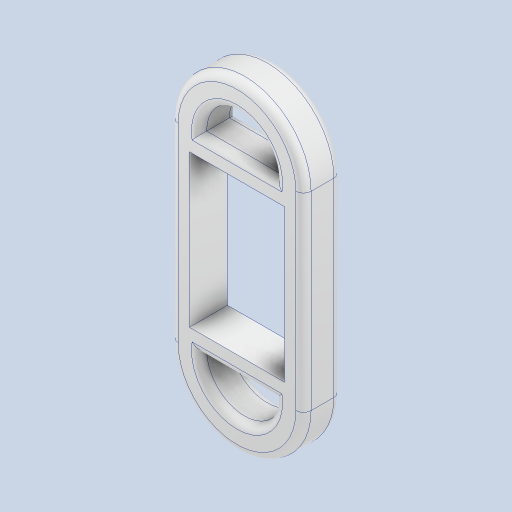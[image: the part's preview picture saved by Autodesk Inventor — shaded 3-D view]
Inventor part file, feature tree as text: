
AUTODESK INVENTOR PART (.ipt)
format: ipt  version: 2024 (Build 280153000, 153)  size: 239,104 bytes
history: native  units: mm
features: other x1, extrude x1, fillet x1, sketch x1
ambient origin geometry x8: Origin, YZ Plane, XZ Plane, XY Plane, X Axis, Y Axis, Z Axis, Center Point
bodies: Body1 (feature_tree)
feature tree (4):
  other  "Sólido1"
  extrude  "Extrusión1"  Depth=4.0mm
  fillet  "Empalme1"  Radius=15.0mm
  sketch  "Boceto1"  dims[d0=170.0mm d1=70.0mm d2=15.0mm d3=20.0mm d4=40.0mm d6=80.0mm d7=10.0mm d8=10.0mm d9=20.0mm d10=0.0mm d11=4.0mm]
